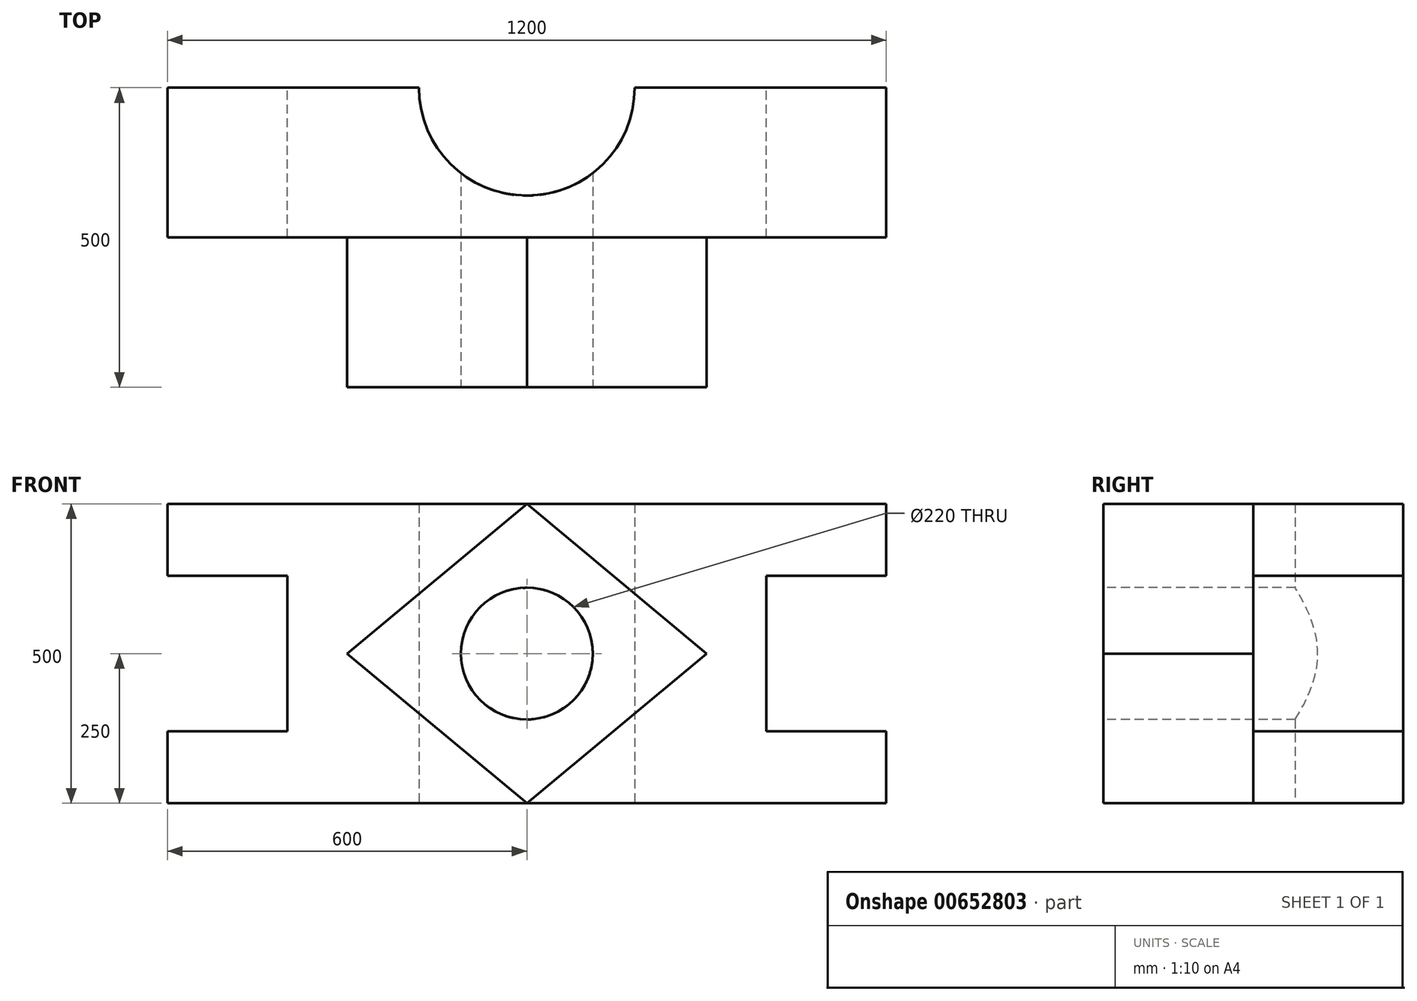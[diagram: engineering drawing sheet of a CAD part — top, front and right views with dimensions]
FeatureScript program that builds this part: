
annotation { "Feature Type Name" : "Feature", "Feature Type Description" : "" }
export const myFeature = defineFeature(function(context is Context, id is Id, definition is map)
    precondition{}
    {
        {
            var Q0;
            Q0=qCreatedBy(makeId("Front.planeOp"),FACE);
            var sketch = newSketch(context, id + "F0", { "sketchPlane" : qUnion([Q0])});
            skLineSegment(sketch, "E0.bottom", {"start": v(-600, -250) * mm, "end": v(600, -250) * mm});
            skLineSegment(sketch, "E0.top", {"start": v(-600, 250) * mm, "end": v(600, 250) * mm});
            skLineSegment(sketch, "E0.left", {"start": v(-600, -250) * mm, "end": v(-600, 250) * mm});
            skLineSegment(sketch, "E0.right", {"start": v(600, -250) * mm, "end": v(600, 250) * mm});
            skPoint(sketch, "E0.middle", {"position": v(0, 0) * mm});
            skPoint(sketch, "E1.middle", {"position": v(-600, 0) * mm});
            skPoint(sketch, "E2.middle", {"position": v(600, 0) * mm});
            skSolve(sketch);
        }
        {
            var Q0;
            Q0=qSketchRegion(id+"F0",true);
            extrude(context, id + "F1", {"entities" : qUnion([Q0]), "depth" : 250 * mm, "offsetDistance" : 25 * mm});
        }
        {
            var Q0;
            Q0=makeQuery(id+"F1.opExtrude","CAP_FACE",FACE,{"disambiguationData":[OSD([sQuery(id+"F0.wireOp",EDGE,"E0.bottom"),sQuery(id+"F0.wireOp",EDGE,"E0.top"),sQuery(id+"F0.wireOp",EDGE,"E0.left"),sQuery(id+"F0.wireOp",EDGE,"E0.right")])],"isStart":true});
            var sketch = newSketch(context, id + "F2", { "sketchPlane" : qUnion([Q0])});
            skLineSegment(sketch, "E3.bottom", {"start": v(-800, -130) * mm, "end": v(-400, -130) * mm});
            skLineSegment(sketch, "E3.top", {"start": v(-800, 130) * mm, "end": v(-400, 130) * mm});
            skLineSegment(sketch, "E3.left", {"start": v(-800, -130) * mm, "end": v(-800, 130) * mm});
            skLineSegment(sketch, "E3.right", {"start": v(-400, -130) * mm, "end": v(-400, 130) * mm});
            skPoint(sketch, "E3.middle", {"position": v(-600, 0) * mm});
            skLineSegment(sketch, "E4.bottom", {"start": v(400, -130) * mm, "end": v(800, -130) * mm});
            skLineSegment(sketch, "E4.top", {"start": v(400, 130) * mm, "end": v(800, 130) * mm});
            skLineSegment(sketch, "E4.left", {"start": v(400, -130) * mm, "end": v(400, 130) * mm});
            skLineSegment(sketch, "E4.right", {"start": v(800, -130) * mm, "end": v(800, 130) * mm});
            skPoint(sketch, "E4.middle", {"position": v(600, 0) * mm});
            skSolve(sketch);
        }
        {
            var Q0;
            Q0=qSketchRegion(id+"F2",true);
            extrude(context, id + "F3", {"entities" : qUnion([Q0]), "operationType" : NewBodyOperationType.REMOVE, "endBound" : BoundingType.THROUGH_ALL, "oppositeDirection" : true, "depth" : 25 * mm, "offsetDistance" : 25 * mm});
        }
        {
            var Q0;
            Q0=makeQuery(id+"F1.opExtrude","CAP_FACE",FACE,{"disambiguationData":[OSD([sQuery(id+"F0.wireOp",EDGE,"E0.bottom"),sQuery(id+"F0.wireOp",EDGE,"E0.top"),sQuery(id+"F0.wireOp",EDGE,"E0.left"),sQuery(id+"F0.wireOp",EDGE,"E0.right")])],"isStart":false});
            var sketch = newSketch(context, id + "F4", { "sketchPlane" : qUnion([Q0])});
            skPoint(sketch, "E5.middle", {"position": v(0, 0) * mm});
            skLineSegment(sketch, "E6", {"start": v(-300, 0) * mm, "end": v(0, -250) * mm});
            skLineSegment(sketch, "E7", {"start": v(0, -250) * mm, "end": v(300, 0) * mm});
            skLineSegment(sketch, "E8", {"start": v(300, 0) * mm, "end": v(0, 250) * mm});
            skLineSegment(sketch, "E9", {"start": v(0, 250) * mm, "end": v(-300, 0) * mm});
            skSolve(sketch);
        }
        {
            var Q0;
            Q0=qSketchRegion(id+"F4",true);
            extrude(context, id + "F5", {"entities" : qUnion([Q0]), "operationType" : NewBodyOperationType.ADD, "depth" : 250 * mm, "offsetDistance" : 25 * mm});
        }
        {
            var Q0;
            Q0=makeQuery(id+"F5.opExtrude","CAP_FACE",FACE,{"disambiguationData":[OSD([sQuery(id+"F4.wireOp",EDGE,"E6"),sQuery(id+"F4.wireOp",EDGE,"E7"),sQuery(id+"F4.wireOp",EDGE,"E8"),sQuery(id+"F4.wireOp",EDGE,"E9")])],"isStart":false});
            var sketch = newSketch(context, id + "F6", { "sketchPlane" : qUnion([Q0])});
            skCircle(sketch, "E10", {"center": v(0, 0) * mm, "radius": 110 * mm});
            skSolve(sketch);
        }
        {
            var Q0;
            Q0=qSketchRegion(id+"F6",true);
            extrude(context, id + "F7", {"entities" : qUnion([Q0]), "operationType" : NewBodyOperationType.REMOVE, "endBound" : BoundingType.THROUGH_ALL, "oppositeDirection" : true, "depth" : 25 * mm, "offsetDistance" : 25 * mm});
        }
        {
            var Q0;
            Q0=makeQuery(id+"F1.opExtrude","SWEPT_FACE",FACE,{"disambiguationData":[OSD([sQuery(id+"F0.wireOp",EDGE,"E0.bottom")])]});
            var sketch = newSketch(context, id + "F8", { "sketchPlane" : qUnion([Q0])});
            skCircle(sketch, "E11", {"center": v(0, 0) * mm, "radius": 180 * mm});
            skSolve(sketch);
        }
        {
            var Q0;
            Q0=qSketchRegion(id+"F8",true);
            extrude(context, id + "F9", {"entities" : qUnion([Q0]), "operationType" : NewBodyOperationType.REMOVE, "endBound" : BoundingType.THROUGH_ALL, "oppositeDirection" : true, "depth" : 25 * mm, "offsetDistance" : 25 * mm});
        }
    });
